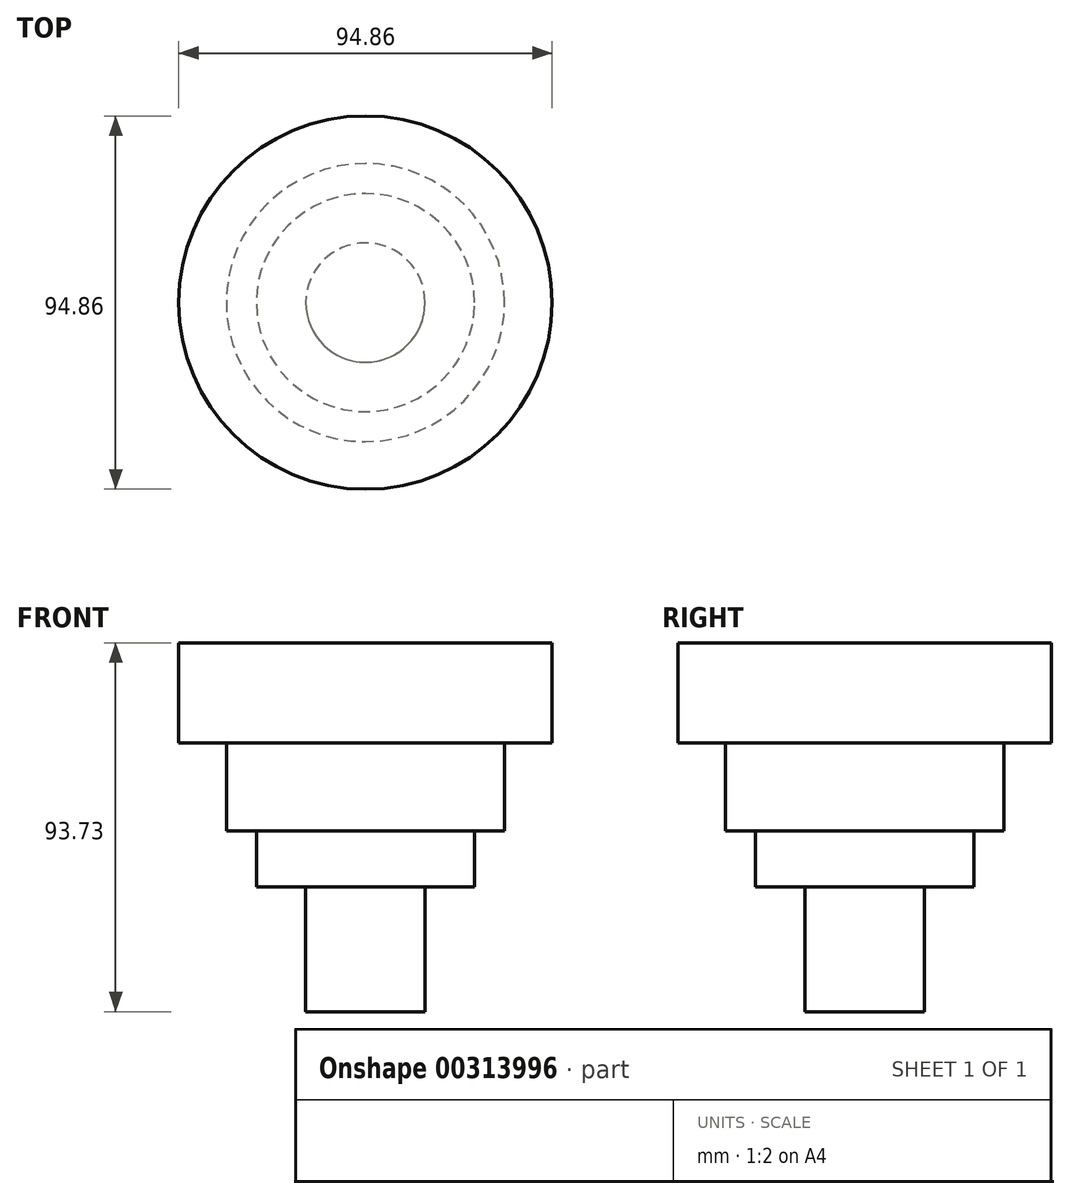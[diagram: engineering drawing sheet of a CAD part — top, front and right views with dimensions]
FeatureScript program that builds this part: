
annotation { "Feature Type Name" : "Feature", "Feature Type Description" : "" }
export const myFeature = defineFeature(function(context is Context, id is Id, definition is map)
    precondition{}
    {
        {
            var Q0;
            Q0=qCreatedBy(makeId("Top.planeOp"),FACE);
            var sketch = newSketch(context, id + "F0", { "sketchPlane" : qUnion([Q0])});
            skCircle(sketch, "E0", {"center": v(0, 0) * mm, "radius": 47.43 * mm});
            skSolve(sketch);
        }
        {
            var Q0;
            Q0 = qSketchRegion(id + "F0", true);
            extrude(context, id + "F1", {"entities" : qUnion([Q0]), "depth" : 25.4 * mm});
        }
        {
            var Q0;
            Q0=qCreatedBy(makeId("Top.planeOp"),FACE);
            var sketch = newSketch(context, id + "F2", { "sketchPlane" : qUnion([Q0])});
            skCircle(sketch, "E1", {"center": v(0, 0) * mm, "radius": 35.34 * mm});
            skSolve(sketch);
        }
        {
            var Q0;
            Q0 = qSketchRegion(id + "F2", true);
            extrude(context, id + "F3", {"entities" : qUnion([Q0]), "operationType" : NewBodyOperationType.ADD, "oppositeDirection" : true, "depth" : 22.35 * mm});
        }
        {
            var Q0;
            Q0=makeQuery(id+"F3.opExtrude","CAP_FACE",FACE,{"disambiguationData":[OSD([sQuery(id+"F2.wireOp",EDGE,"E1")])],"isStart":false});
            var sketch = newSketch(context, id + "F4", { "sketchPlane" : qUnion([Q0])});
            skCircle(sketch, "E2", {"center": v(0, 0) * mm, "radius": 27.72 * mm});
            skSolve(sketch);
        }
        {
            var Q0;
            Q0=makeQuery(id+"F4.imprint","IMPRINT",FACE,{"disambiguationData":[TD([[makeQuery(id+"F4.imprint","IMPRINT",EDGE,{"derivedFrom":sQuery(id+"F4.wireOp",EDGE,"E2")}),1.0]])]});
            extrude(context, id + "F5", {"entities" : qUnion([Q0]), "operationType" : NewBodyOperationType.ADD, "depth" : 14.22 * mm});
        }
        {
            var Q0;
            Q0=qCreatedBy(makeId("Top.planeOp"),FACE);
            var sketch = newSketch(context, id + "F6", { "sketchPlane" : qUnion([Q0])});
            skCircle(sketch, "E3", {"center": v(0, 0) * mm, "radius": 15.16 * mm});
            skSolve(sketch);
        }
        {
            var Q0;
            Q0 = qSketchRegion(id + "F6", true);
            extrude(context, id + "F7", {"entities" : qUnion([Q0]), "operationType" : NewBodyOperationType.ADD, "oppositeDirection" : true, "depth" : 68.33 * mm});
        }
    });
